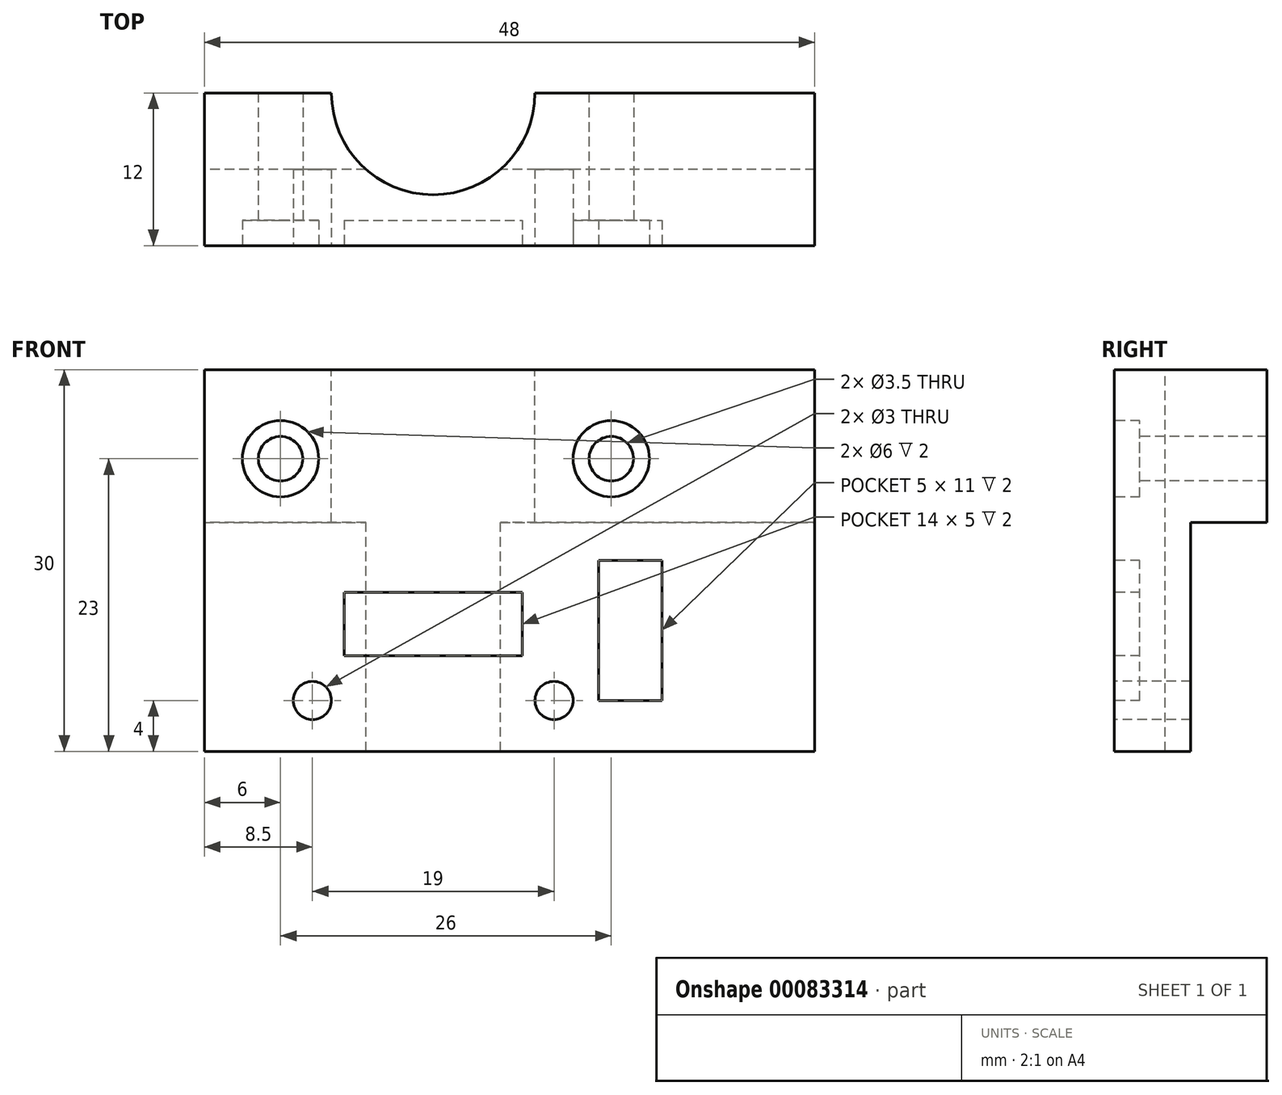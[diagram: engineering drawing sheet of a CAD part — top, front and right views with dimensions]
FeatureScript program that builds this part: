
annotation { "Feature Type Name" : "Feature", "Feature Type Description" : "" }
export const myFeature = defineFeature(function(context is Context, id is Id, definition is map)
    precondition{}
    {
        {
            var Q0;
            Q0=qCreatedBy(makeId("Front.planeOp"),FACE);
            var sketch = newSketch(context, id + "F0", { "sketchPlane" : qUnion([Q0])});
            skLineSegment(sketch, "E0.bottom", {"start": v(24, 15) * mm, "end": v(-24, 15) * mm});
            skLineSegment(sketch, "E0.top", {"start": v(24, -15) * mm, "end": v(-24, -15) * mm});
            skLineSegment(sketch, "E0.left", {"start": v(24, 15) * mm, "end": v(24, -15) * mm});
            skLineSegment(sketch, "E0.right", {"start": v(-24, 15) * mm, "end": v(-24, -15) * mm});
            skPoint(sketch, "E0.middle", {"position": v(0, 0) * mm});
            skLineSegment(sketch, "E1", {"start": v(-24, -13.5) * mm, "end": v(24, -13.5) * mm, "construction": true});
            skLineSegment(sketch, "E2", {"start": v(-24, -11) * mm, "end": v(24, -11) * mm, "construction": true});
            skLineSegment(sketch, "E3", {"start": v(-24, 8) * mm, "end": v(24, 8) * mm, "construction": true});
            skCircle(sketch, "E4", {"center": v(-15.5, -11) * mm, "radius": 1.5 * mm});
            skCircle(sketch, "E5", {"center": v(3.5, -11) * mm, "radius": 1.5 * mm});
            skLineSegment(sketch, "E6.bottom", {"start": v(7, -11) * mm, "end": v(12, -11) * mm});
            skLineSegment(sketch, "E6.top", {"start": v(7, 0) * mm, "end": v(12, 0) * mm});
            skLineSegment(sketch, "E6.left", {"start": v(7, -11) * mm, "end": v(7, 0) * mm});
            skLineSegment(sketch, "E6.right", {"start": v(12, -11) * mm, "end": v(12, 0) * mm});
            skLineSegment(sketch, "E7.bottom", {"start": v(-13, -7.5) * mm, "end": v(1, -7.5) * mm});
            skLineSegment(sketch, "E7.top", {"start": v(-13, -2.5) * mm, "end": v(1, -2.5) * mm});
            skLineSegment(sketch, "E7.left", {"start": v(-13, -7.5) * mm, "end": v(-13, -2.5) * mm});
            skLineSegment(sketch, "E7.right", {"start": v(1, -7.5) * mm, "end": v(1, -2.5) * mm});
            skLineSegment(sketch, "E8", {"start": v(0, 20.68) * mm, "end": v(0, -38.74) * mm, "construction": true});
            skCircle(sketch, "E9", {"center": v(-18, 8) * mm, "radius": 1.75 * mm});
            skCircle(sketch, "E10", {"center": v(8, 8) * mm, "radius": 1.75 * mm});
            skCircle(sketch, "E11", {"center": v(-18, 8) * mm, "radius": 3 * mm});
            skCircle(sketch, "E12", {"center": v(8, 8) * mm, "radius": 3 * mm});
            skSolve(sketch);
        }
        {
            var Q0;
            Q0=makeQuery(id+"F0.imprint","IMPRINT",FACE,{"disambiguationData":[TD([[makeQuery(id+"F0.imprint","IMPRINT",EDGE,{"derivedFrom":sQuery(id+"F0.wireOp",EDGE,"E0.bottom")}),1.0]])]});
            var Q1;
            Q1=makeQuery(id+"F0.imprint","IMPRINT",FACE,{"disambiguationData":[TD([[makeQuery(id+"F0.imprint","IMPRINT",EDGE,{"derivedFrom":sQuery(id+"F0.wireOp",EDGE,"E7.bottom")}),1.0]])]});
            var Q2;
            Q2=makeQuery(id+"F0.imprint","IMPRINT",FACE,{"disambiguationData":[TD([[makeQuery(id+"F0.imprint","IMPRINT",EDGE,{"derivedFrom":sQuery(id+"F0.wireOp",EDGE,"E6.bottom")}),1.0]])]});
            var Q3;
            Q3=makeQuery(id+"F0.imprint","IMPRINT",FACE,{"disambiguationData":[TD([[makeQuery(id+"F0.imprint","IMPRINT",EDGE,{"derivedFrom":sQuery(id+"F0.wireOp",EDGE,"E10")}),-1.0]])]});
            var Q4;
            Q4=makeQuery(id+"F0.imprint","IMPRINT",FACE,{"disambiguationData":[TD([[makeQuery(id+"F0.imprint","IMPRINT",EDGE,{"derivedFrom":sQuery(id+"F0.wireOp",EDGE,"E9")}),-1.0]])]});
            extrude(context, id + "F1", {"entities" : qUnion([Q0, Q1, Q2, Q3, Q4]), "oppositeDirection" : true, "depth" : 6 * mm});
        }
        {
            var Q0;
            Q0=makeQuery(id+"F0.imprint","IMPRINT",FACE,{"disambiguationData":[TD([[makeQuery(id+"F0.imprint","IMPRINT",EDGE,{"derivedFrom":sQuery(id+"F0.wireOp",EDGE,"E6.bottom")}),1.0]])]});
            var Q1;
            Q1=makeQuery(id+"F0.imprint","IMPRINT",FACE,{"disambiguationData":[TD([[makeQuery(id+"F0.imprint","IMPRINT",EDGE,{"derivedFrom":sQuery(id+"F0.wireOp",EDGE,"E7.bottom")}),1.0]])]});
            var Q2;
            Q2=makeQuery(id+"F0.imprint","IMPRINT",FACE,{"disambiguationData":[TD([[makeQuery(id+"F0.imprint","IMPRINT",EDGE,{"derivedFrom":sQuery(id+"F0.wireOp",EDGE,"E9")}),-1.0]])]});
            var Q3;
            Q3=makeQuery(id+"F0.imprint","IMPRINT",FACE,{"disambiguationData":[TD([[makeQuery(id+"F0.imprint","IMPRINT",EDGE,{"derivedFrom":sQuery(id+"F0.wireOp",EDGE,"E10")}),-1.0]])]});
            extrude(context, id + "F2", {"entities" : qUnion([Q0, Q1, Q2, Q3]), "operationType" : NewBodyOperationType.REMOVE, "oppositeDirection" : true, "depth" : 2 * mm, "offsetDistance" : 25 * mm});
        }
        {
            var Q0;
            Q0=makeQuery(id+"F1.opExtrude","CAP_FACE",FACE,{"disambiguationData":[OSD([sQuery(id+"F0.wireOp",EDGE,"E0.bottom"),sQuery(id+"F0.wireOp",EDGE,"E0.top"),sQuery(id+"F0.wireOp",EDGE,"E0.left"),sQuery(id+"F0.wireOp",EDGE,"E0.right"),sQuery(id+"F0.wireOp",EDGE,"E4"),sQuery(id+"F0.wireOp",EDGE,"E5"),sQuery(id+"F0.wireOp",EDGE,"E9"),sQuery(id+"F0.wireOp",EDGE,"E10")])],"isStart":false});
            var sketch = newSketch(context, id + "F3", { "sketchPlane" : qUnion([Q0])});
            skCircle(sketch, "E13.cCircle", {"center": v(-3.5, -11) * mm, "radius": 3 * mm, "construction": true});
            skLineSegment(sketch, "E13.0", {"start": v(-6.5, -9.27) * mm, "end": v(-3.5, -7.54) * mm});
            skLineSegment(sketch, "E13.1", {"start": v(-3.5, -7.54) * mm, "end": v(-0.5, -9.27) * mm});
            skLineSegment(sketch, "E13.2", {"start": v(-0.5, -9.27) * mm, "end": v(-0.5, -12.73) * mm});
            skLineSegment(sketch, "E13.3", {"start": v(-0.5, -12.73) * mm, "end": v(-3.5, -14.46) * mm});
            skLineSegment(sketch, "E13.4", {"start": v(-3.5, -14.46) * mm, "end": v(-6.5, -12.73) * mm});
            skLineSegment(sketch, "E13.5", {"start": v(-6.5, -12.73) * mm, "end": v(-6.5, -9.27) * mm});
            skPoint(sketch, "E13.0.midPoint", {"position": v(-5, -8.4) * mm});
            skCircle(sketch, "E14.cCircle", {"center": v(15.5, -11) * mm, "radius": 3 * mm, "construction": true});
            skLineSegment(sketch, "E14.0", {"start": v(12.5, -12.73) * mm, "end": v(12.5, -9.27) * mm});
            skLineSegment(sketch, "E14.1", {"start": v(12.5, -9.27) * mm, "end": v(15.5, -7.54) * mm});
            skLineSegment(sketch, "E14.2", {"start": v(15.5, -7.54) * mm, "end": v(18.5, -9.27) * mm});
            skLineSegment(sketch, "E14.3", {"start": v(18.5, -9.27) * mm, "end": v(18.5, -12.73) * mm});
            skLineSegment(sketch, "E14.4", {"start": v(18.5, -12.73) * mm, "end": v(15.5, -14.46) * mm});
            skLineSegment(sketch, "E14.5", {"start": v(15.5, -14.46) * mm, "end": v(12.5, -12.73) * mm});
            skPoint(sketch, "E14.0.midPoint", {"position": v(12.5, -11) * mm});
            skSolve(sketch);
        }
        {
            var Q0;
            Q0=makeQuery(id+"F1.opExtrude","SWEPT_FACE",FACE,{"disambiguationData":[OSD([sQuery(id+"F0.wireOp",EDGE,"E0.bottom")])]});
            var sketch = newSketch(context, id + "F4", { "sketchPlane" : qUnion([Q0])});
            skLineSegment(sketch, "E15.bottom", {"start": v(-24, 6) * mm, "end": v(24, 6) * mm});
            skLineSegment(sketch, "E15.top", {"start": v(-24, 12) * mm, "end": v(-14, 12) * mm});
            skLineSegment(sketch, "E15.left", {"start": v(-24, 6) * mm, "end": v(-24, 12) * mm});
            skLineSegment(sketch, "E15.right", {"start": v(24, 6) * mm, "end": v(24, 12) * mm});
            skArc(sketch, "E16", {"start": v(-14, 12) * mm, "mid": v(-6, 4) * mm, "end": v(2, 12) * mm});
            skLineSegment(sketch, "E17.trimOffspring", {"start": v(2, 12) * mm, "end": v(24, 12) * mm});
            skCircle(sketch, "E18", {"center": v(-6, 12) * mm, "radius": 8 * mm});
            skSolve(sketch);
        }
        {
            var Q0;
            {var subQ4=sQuery(id+"F4.wireOp",EDGE,"E15.top");Q0=makeQuery(id+"F4.imprint","IMPRINT",FACE,{"disambiguationData":[TD([[makeQuery(id+"F4.imprint","IMPRINT",EDGE,{"derivedFrom":subQ4}),-1.0]])]});}
            var Q1;
            {var subQ0=sQuery(id+"F4.wireOp",EDGE,"E15.right");Q1=makeQuery(id+"F4.imprint","IMPRINT",FACE,{"disambiguationData":[TD([[makeQuery(id+"F4.imprint","IMPRINT",EDGE,{"derivedFrom":subQ0}),1.0]])]});}
            extrude(context, id + "F5", {"entities" : qUnion([Q0, Q1]), "operationType" : NewBodyOperationType.ADD, "oppositeDirection" : true, "depth" : 12 * mm, "offsetDistance" : 25 * mm});
        }
        {
            var Q0;
            Q0=makeQuery(id+"F0.imprint","IMPRINT",FACE,{"disambiguationData":[TD([[makeQuery(id+"F0.imprint","IMPRINT",EDGE,{"derivedFrom":sQuery(id+"F0.wireOp",EDGE,"E9")}),1.0]])]});
            var Q1;
            Q1=makeQuery(id+"F0.imprint","IMPRINT",FACE,{"disambiguationData":[TD([[makeQuery(id+"F0.imprint","IMPRINT",EDGE,{"derivedFrom":sQuery(id+"F0.wireOp",EDGE,"E10")}),1.0]])]});
            extrude(context, id + "F6", {"entities" : qUnion([Q0, Q1]), "operationType" : NewBodyOperationType.REMOVE, "endBound" : BoundingType.THROUGH_ALL, "oppositeDirection" : true, "depth" : 25 * mm, "offsetDistance" : 25 * mm});
        }
        {
            var Q0;
            {var subQ0=sQuery(id+"F4.wireOp",EDGE,"E18");var subQ1=sQuery(id+"F4.wireOp",EDGE,"E15.bottom");var subQ2=makeQuery(id+"F4.imprint","INTERSECT",VERTEX,{"disambiguationData":[OD(0.0)],"derivedFrom":[subQ1,subQ0]});Q0=makeQuery(id+"F4.imprint","IMPRINT",FACE,{"disambiguationData":[TD([[makeQuery(id+"F4.imprint","IMPRINT",EDGE,{"disambiguationData":[TD([[subQ2,-1.0]])],"derivedFrom":subQ1}),1.0]])]});}
            extrude(context, id + "F7", {"entities" : qUnion([Q0]), "operationType" : NewBodyOperationType.REMOVE, "endBound" : BoundingType.THROUGH_ALL, "oppositeDirection" : true, "depth" : 25 * mm, "offsetDistance" : 25 * mm});
        }
    });
